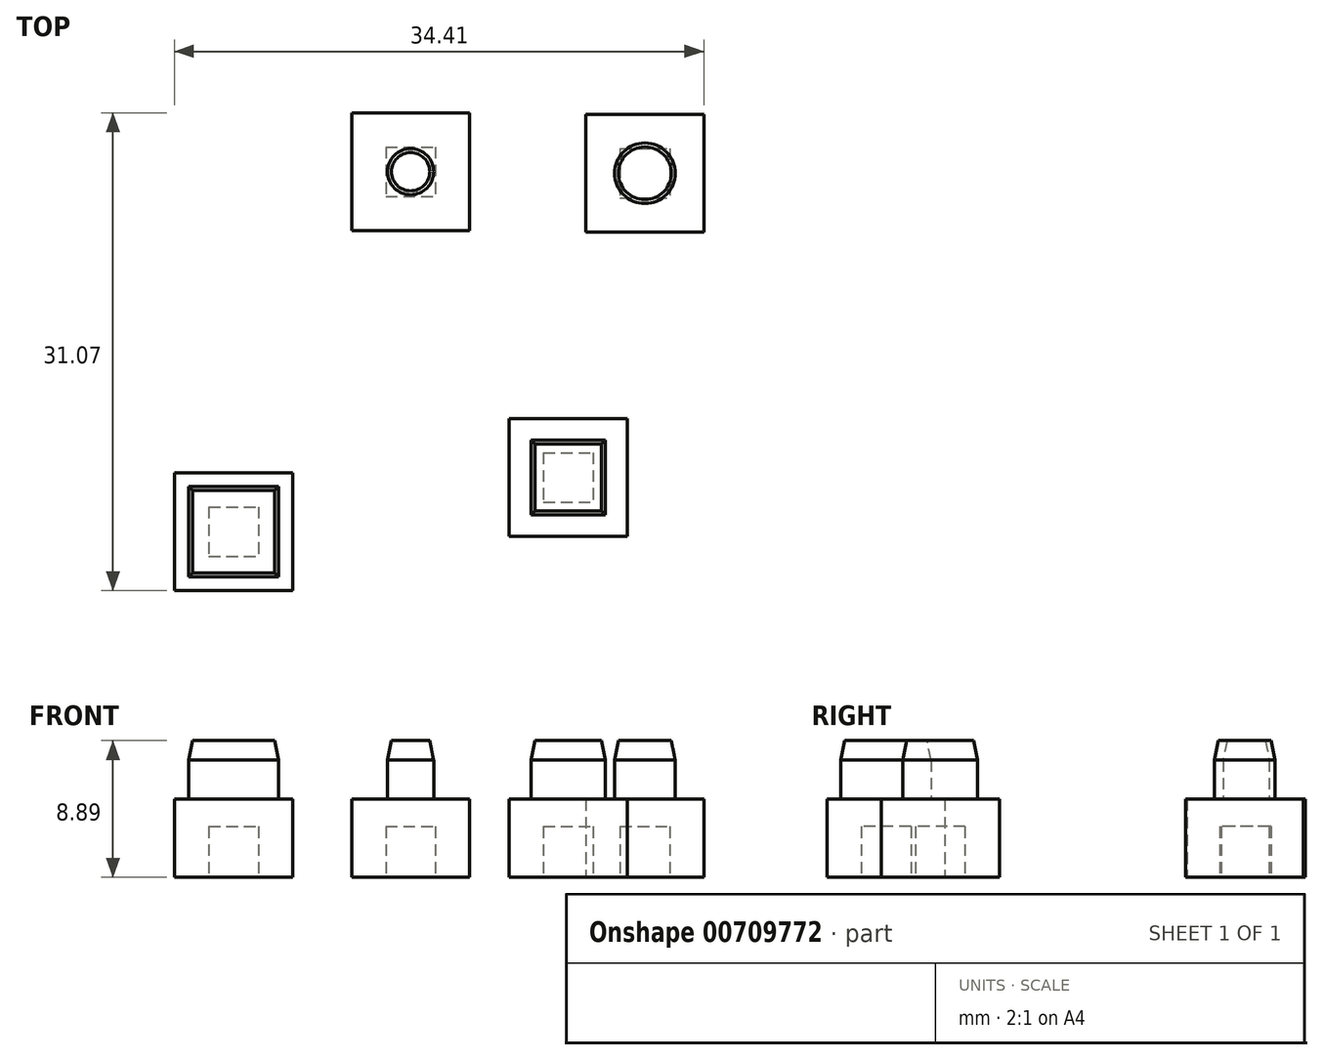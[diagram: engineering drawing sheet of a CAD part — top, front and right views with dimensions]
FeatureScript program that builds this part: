
annotation { "Feature Type Name" : "Feature", "Feature Type Description" : "" }
export const myFeature = defineFeature(function(context is Context, id is Id, definition is map)
    precondition{}
    {
        {
            var Q0;
            Q0=qCreatedBy(makeId("Top.planeOp"),FACE);
            var sketch = newSketch(context, id + "F0", { "sketchPlane" : qUnion([Q0])});
            skLineSegment(sketch, "E0.bottom", {"start": v(13.82, 29.65) * mm, "end": v(17.05, 29.65) * mm});
            skLineSegment(sketch, "E0.top", {"start": v(13.82, 26.43) * mm, "end": v(17.05, 26.43) * mm});
            skLineSegment(sketch, "E0.left", {"start": v(13.82, 29.65) * mm, "end": v(13.82, 26.43) * mm});
            skLineSegment(sketch, "E0.right", {"start": v(17.05, 29.65) * mm, "end": v(17.05, 26.43) * mm});
            skLineSegment(sketch, "E1.bottom", {"start": v(11.6, 24.2) * mm, "end": v(19.27, 24.2) * mm});
            skLineSegment(sketch, "E1.top", {"start": v(11.6, 31.87) * mm, "end": v(19.27, 31.87) * mm});
            skLineSegment(sketch, "E1.left", {"start": v(11.6, 24.2) * mm, "end": v(11.6, 31.87) * mm});
            skLineSegment(sketch, "E1.right", {"start": v(19.27, 24.2) * mm, "end": v(19.27, 31.87) * mm});
            skPoint(sketch, "E2", {"position": v(15.44, 28.04) * mm});
            skCircle(sketch, "E3", {"center": v(15.44, 28.04) * mm, "radius": 1.5 * mm});
            skLineSegment(sketch, "E4.bottom", {"start": v(2.31, 6.25) * mm, "end": v(5.54, 6.25) * mm});
            skLineSegment(sketch, "E4.top", {"start": v(2.31, 3.03) * mm, "end": v(5.54, 3.03) * mm});
            skLineSegment(sketch, "E4.left", {"start": v(2.31, 6.25) * mm, "end": v(2.31, 3.03) * mm});
            skLineSegment(sketch, "E4.right", {"start": v(5.54, 6.25) * mm, "end": v(5.54, 3.03) * mm});
            skLineSegment(sketch, "E5.bottom", {"start": v(0.1, 0.8) * mm, "end": v(7.76, 0.8) * mm});
            skLineSegment(sketch, "E5.top", {"start": v(0.1, 8.47) * mm, "end": v(7.76, 8.47) * mm});
            skLineSegment(sketch, "E5.left", {"start": v(0.1, 0.8) * mm, "end": v(0.1, 8.47) * mm});
            skLineSegment(sketch, "E5.right", {"start": v(7.76, 0.8) * mm, "end": v(7.76, 8.47) * mm});
            skPoint(sketch, "E6", {"position": v(3.93, 4.64) * mm});
            skLineSegment(sketch, "E7.bottom", {"start": v(24.07, 9.78) * mm, "end": v(27.3, 9.78) * mm});
            skLineSegment(sketch, "E7.top", {"start": v(24.07, 6.55) * mm, "end": v(27.3, 6.55) * mm});
            skLineSegment(sketch, "E7.left", {"start": v(24.07, 9.78) * mm, "end": v(24.07, 6.55) * mm});
            skLineSegment(sketch, "E7.right", {"start": v(27.3, 9.78) * mm, "end": v(27.3, 6.55) * mm});
            skLineSegment(sketch, "E8.bottom", {"start": v(21.84, 4.33) * mm, "end": v(29.52, 4.33) * mm});
            skLineSegment(sketch, "E8.top", {"start": v(21.84, 12) * mm, "end": v(29.52, 12) * mm});
            skLineSegment(sketch, "E8.left", {"start": v(21.84, 4.33) * mm, "end": v(21.84, 12) * mm});
            skLineSegment(sketch, "E8.right", {"start": v(29.52, 4.33) * mm, "end": v(29.52, 12) * mm});
            skPoint(sketch, "E9", {"position": v(25.68, 8.16) * mm});
            skLineSegment(sketch, "E10.bottom", {"start": v(29.05, 29.55) * mm, "end": v(32.28, 29.55) * mm});
            skLineSegment(sketch, "E10.top", {"start": v(29.05, 26.33) * mm, "end": v(32.28, 26.33) * mm});
            skLineSegment(sketch, "E10.left", {"start": v(29.05, 29.55) * mm, "end": v(29.05, 26.33) * mm});
            skLineSegment(sketch, "E10.right", {"start": v(32.28, 29.55) * mm, "end": v(32.28, 26.33) * mm});
            skLineSegment(sketch, "E11.bottom", {"start": v(26.83, 24.1) * mm, "end": v(34.5, 24.1) * mm});
            skLineSegment(sketch, "E11.top", {"start": v(26.83, 31.78) * mm, "end": v(34.5, 31.78) * mm});
            skLineSegment(sketch, "E11.left", {"start": v(26.83, 24.1) * mm, "end": v(26.83, 31.78) * mm});
            skLineSegment(sketch, "E11.right", {"start": v(34.5, 24.1) * mm, "end": v(34.5, 31.78) * mm});
            skPoint(sketch, "E12", {"position": v(30.66, 27.94) * mm});
            skCircle(sketch, "E13", {"center": v(30.66, 27.94) * mm, "radius": 1.97 * mm});
            skLineSegment(sketch, "E14.bottom", {"start": v(6.86, 7.57) * mm, "end": v(1, 7.57) * mm});
            skLineSegment(sketch, "E14.top", {"start": v(6.86, 1.7) * mm, "end": v(1, 1.7) * mm});
            skLineSegment(sketch, "E14.left", {"start": v(6.86, 7.57) * mm, "end": v(6.86, 1.7) * mm});
            skLineSegment(sketch, "E14.right", {"start": v(1, 7.57) * mm, "end": v(1, 1.7) * mm});
            skLineSegment(sketch, "E15.bottom", {"start": v(28.1, 10.59) * mm, "end": v(23.25, 10.59) * mm});
            skLineSegment(sketch, "E15.top", {"start": v(28.1, 5.74) * mm, "end": v(23.25, 5.74) * mm});
            skLineSegment(sketch, "E15.left", {"start": v(28.1, 10.59) * mm, "end": v(28.1, 5.74) * mm});
            skLineSegment(sketch, "E15.right", {"start": v(23.25, 10.59) * mm, "end": v(23.25, 5.74) * mm});
            skSolve(sketch);
        }
        {
            var Q0;
            Q0=makeQuery(id+"F0.imprint","IMPRINT",FACE,{"disambiguationData":[TD([[makeQuery(id+"F0.imprint","IMPRINT",EDGE,{"derivedFrom":sQuery(id+"F0.wireOp",EDGE,"E4.bottom")}),1.0]])]});
            var Q1;
            Q1=makeQuery(id+"F0.imprint","IMPRINT",FACE,{"disambiguationData":[TD([[makeQuery(id+"F0.imprint","IMPRINT",EDGE,{"derivedFrom":sQuery(id+"F0.wireOp",EDGE,"E11.bottom")}),1.0]])]});
            var Q2;
            Q2=makeQuery(id+"F0.imprint","IMPRINT",FACE,{"disambiguationData":[TD([[makeQuery(id+"F0.imprint","IMPRINT",EDGE,{"derivedFrom":sQuery(id+"F0.wireOp",EDGE,"E3")}),1.0]])]});
            var Q3;
            Q3=makeQuery(id+"F0.imprint","IMPRINT",FACE,{"disambiguationData":[TD([[makeQuery(id+"F0.imprint","IMPRINT",EDGE,{"derivedFrom":sQuery(id+"F0.wireOp",EDGE,"E0.bottom")}),1.0]])]});
            var Q4;
            {var subQ0=sQuery(id+"F0.wireOp",EDGE,"E13");var subQ7=sQuery(id+"F0.wireOp",EDGE,"E10.bottom");var subQ8=makeQuery(id+"F0.imprint","INTERSECT",VERTEX,{"disambiguationData":[OD(0.0)],"derivedFrom":[subQ7,subQ0]});Q4=makeQuery(id+"F0.imprint","IMPRINT",FACE,{"disambiguationData":[TD([[makeQuery(id+"F0.imprint","IMPRINT",EDGE,{"disambiguationData":[TD([[subQ8,-1.0]])],"derivedFrom":subQ7}),-1.0]])]});}
            var Q5;
            Q5=makeQuery(id+"F0.imprint","IMPRINT",FACE,{"disambiguationData":[TD([[makeQuery(id+"F0.imprint","IMPRINT",EDGE,{"derivedFrom":sQuery(id+"F0.wireOp",EDGE,"E8.bottom")}),1.0]])]});
            var Q6;
            Q6=makeQuery(id+"F0.imprint","IMPRINT",FACE,{"disambiguationData":[TD([[makeQuery(id+"F0.imprint","IMPRINT",EDGE,{"derivedFrom":sQuery(id+"F0.wireOp",EDGE,"E7.bottom")}),-1.0]])]});
            var Q7;
            Q7=makeQuery(id+"F0.imprint","IMPRINT",FACE,{"disambiguationData":[TD([[makeQuery(id+"F0.imprint","IMPRINT",EDGE,{"derivedFrom":sQuery(id+"F0.wireOp",EDGE,"E5.bottom")}),1.0]])]});
            var Q8;
            Q8=makeQuery(id+"F0.imprint","IMPRINT",FACE,{"disambiguationData":[TD([[makeQuery(id+"F0.imprint","IMPRINT",EDGE,{"derivedFrom":sQuery(id+"F0.wireOp",EDGE,"E7.bottom")}),1.0]])]});
            var Q9;
            Q9=makeQuery(id+"F0.imprint","IMPRINT",FACE,{"disambiguationData":[TD([[makeQuery(id+"F0.imprint","IMPRINT",EDGE,{"derivedFrom":sQuery(id+"F0.wireOp",EDGE,"E4.bottom")}),-1.0]])]});
            var Q10;
            {var subQ0=sQuery(id+"F0.wireOp",EDGE,"E13");var subQ1=sQuery(id+"F0.wireOp",EDGE,"E10.left");var subQ2=makeQuery(id+"F0.imprint","INTERSECT",VERTEX,{"disambiguationData":[OD(0.0)],"derivedFrom":[subQ1,subQ0]});Q10=makeQuery(id+"F0.imprint","IMPRINT",FACE,{"disambiguationData":[TD([[makeQuery(id+"F0.imprint","IMPRINT",EDGE,{"disambiguationData":[TD([[subQ2,-1.0]])],"derivedFrom":subQ1}),-1.0]])]});}
            var Q11;
            Q11=makeQuery(id+"F0.imprint","IMPRINT",FACE,{"disambiguationData":[TD([[makeQuery(id+"F0.imprint","IMPRINT",EDGE,{"derivedFrom":sQuery(id+"F0.wireOp",EDGE,"E0.bottom")}),-1.0]])]});
            var Q12;
            {var subQ0=sQuery(id+"F0.wireOp",EDGE,"E13");var subQ1=sQuery(id+"F0.wireOp",EDGE,"E10.right");var subQ2=makeQuery(id+"F0.imprint","INTERSECT",VERTEX,{"disambiguationData":[OD(0.0)],"derivedFrom":[subQ1,subQ0]});Q12=makeQuery(id+"F0.imprint","IMPRINT",FACE,{"disambiguationData":[TD([[makeQuery(id+"F0.imprint","IMPRINT",EDGE,{"disambiguationData":[TD([[subQ2,-1.0]])],"derivedFrom":subQ1}),1.0]])]});}
            var Q13;
            {var subQ0=sQuery(id+"F0.wireOp",EDGE,"E13");var subQ1=sQuery(id+"F0.wireOp",EDGE,"E10.top");var subQ2=makeQuery(id+"F0.imprint","INTERSECT",VERTEX,{"disambiguationData":[OD(0.0)],"derivedFrom":[subQ1,subQ0]});Q13=makeQuery(id+"F0.imprint","IMPRINT",FACE,{"disambiguationData":[TD([[makeQuery(id+"F0.imprint","IMPRINT",EDGE,{"disambiguationData":[TD([[subQ2,-1.0]])],"derivedFrom":subQ1}),-1.0]])]});}
            var Q14;
            {var subQ0=sQuery(id+"F0.wireOp",EDGE,"E13");var subQ1=sQuery(id+"F0.wireOp",EDGE,"E10.bottom");var subQ2=makeQuery(id+"F0.imprint","INTERSECT",VERTEX,{"disambiguationData":[OD(0.0)],"derivedFrom":[subQ1,subQ0]});Q14=makeQuery(id+"F0.imprint","IMPRINT",FACE,{"disambiguationData":[TD([[makeQuery(id+"F0.imprint","IMPRINT",EDGE,{"disambiguationData":[TD([[subQ2,-1.0]])],"derivedFrom":subQ1}),1.0]])]});}
            var Q15;
            {var subQ0=sQuery(id+"F0.wireOp",EDGE,"E10.left");var subQ1=sQuery(id+"F0.wireOp",EDGE,"E10.top");var subQ2=makeQuery(id+"F0.imprint","INTERSECT",VERTEX,{"derivedFrom":[subQ1,subQ0]});Q15=makeQuery(id+"F0.imprint","IMPRINT",FACE,{"disambiguationData":[TD([[makeQuery(id+"F0.imprint","IMPRINT",EDGE,{"disambiguationData":[TD([[subQ2,-1.0]])],"derivedFrom":subQ1}),1.0]])]});}
            var Q16;
            {var subQ0=sQuery(id+"F0.wireOp",EDGE,"E10.left");var subQ1=sQuery(id+"F0.wireOp",EDGE,"E10.bottom");var subQ2=makeQuery(id+"F0.imprint","INTERSECT",VERTEX,{"derivedFrom":[subQ1,subQ0]});Q16=makeQuery(id+"F0.imprint","IMPRINT",FACE,{"disambiguationData":[TD([[makeQuery(id+"F0.imprint","IMPRINT",EDGE,{"disambiguationData":[TD([[subQ2,-1.0]])],"derivedFrom":subQ1}),-1.0]])]});}
            var Q17;
            {var subQ0=sQuery(id+"F0.wireOp",EDGE,"E10.right");var subQ1=sQuery(id+"F0.wireOp",EDGE,"E10.bottom");var subQ2=makeQuery(id+"F0.imprint","INTERSECT",VERTEX,{"derivedFrom":[subQ1,subQ0]});Q17=makeQuery(id+"F0.imprint","IMPRINT",FACE,{"disambiguationData":[TD([[makeQuery(id+"F0.imprint","IMPRINT",EDGE,{"disambiguationData":[TD([[subQ2,1.0]])],"derivedFrom":subQ1}),-1.0]])]});}
            var Q18;
            {var subQ0=sQuery(id+"F0.wireOp",EDGE,"E10.right");var subQ1=sQuery(id+"F0.wireOp",EDGE,"E10.top");var subQ2=makeQuery(id+"F0.imprint","INTERSECT",VERTEX,{"derivedFrom":[subQ1,subQ0]});Q18=makeQuery(id+"F0.imprint","IMPRINT",FACE,{"disambiguationData":[TD([[makeQuery(id+"F0.imprint","IMPRINT",EDGE,{"disambiguationData":[TD([[subQ2,1.0]])],"derivedFrom":subQ1}),1.0]])]});}
            extrude(context, id + "F1", {"entities" : qUnion([Q0, Q1, Q2, Q3, Q4, Q5, Q6, Q7, Q8, Q9, Q10, Q11, Q12, Q13, Q14, Q15, Q16, Q17, Q18]), "depth" : 5.08 * mm, "offsetDistance" : 25.4 * mm});
        }
        {
            var Q0;
            {var subQ0=sQuery(id+"F0.wireOp",EDGE,"E13");var subQ1=sQuery(id+"F0.wireOp",EDGE,"E10.top");var subQ2=makeQuery(id+"F0.imprint","INTERSECT",VERTEX,{"disambiguationData":[OD(0.0)],"derivedFrom":[subQ1,subQ0]});Q0=makeQuery(id+"F0.imprint","IMPRINT",FACE,{"disambiguationData":[TD([[makeQuery(id+"F0.imprint","IMPRINT",EDGE,{"disambiguationData":[TD([[subQ2,-1.0]])],"derivedFrom":subQ1}),-1.0]])]});}
            var Q1;
            {var subQ0=sQuery(id+"F0.wireOp",EDGE,"E13");var subQ7=sQuery(id+"F0.wireOp",EDGE,"E10.bottom");var subQ8=makeQuery(id+"F0.imprint","INTERSECT",VERTEX,{"disambiguationData":[OD(0.0)],"derivedFrom":[subQ7,subQ0]});Q1=makeQuery(id+"F0.imprint","IMPRINT",FACE,{"disambiguationData":[TD([[makeQuery(id+"F0.imprint","IMPRINT",EDGE,{"disambiguationData":[TD([[subQ8,-1.0]])],"derivedFrom":subQ7}),-1.0]])]});}
            var Q2;
            {var subQ0=sQuery(id+"F0.wireOp",EDGE,"E13");var subQ1=sQuery(id+"F0.wireOp",EDGE,"E10.left");var subQ2=makeQuery(id+"F0.imprint","INTERSECT",VERTEX,{"disambiguationData":[OD(0.0)],"derivedFrom":[subQ1,subQ0]});Q2=makeQuery(id+"F0.imprint","IMPRINT",FACE,{"disambiguationData":[TD([[makeQuery(id+"F0.imprint","IMPRINT",EDGE,{"disambiguationData":[TD([[subQ2,-1.0]])],"derivedFrom":subQ1}),-1.0]])]});}
            var Q3;
            {var subQ0=sQuery(id+"F0.wireOp",EDGE,"E13");var subQ1=sQuery(id+"F0.wireOp",EDGE,"E10.bottom");var subQ2=makeQuery(id+"F0.imprint","INTERSECT",VERTEX,{"disambiguationData":[OD(0.0)],"derivedFrom":[subQ1,subQ0]});Q3=makeQuery(id+"F0.imprint","IMPRINT",FACE,{"disambiguationData":[TD([[makeQuery(id+"F0.imprint","IMPRINT",EDGE,{"disambiguationData":[TD([[subQ2,-1.0]])],"derivedFrom":subQ1}),1.0]])]});}
            var Q4;
            {var subQ0=sQuery(id+"F0.wireOp",EDGE,"E13");var subQ1=sQuery(id+"F0.wireOp",EDGE,"E10.right");var subQ2=makeQuery(id+"F0.imprint","INTERSECT",VERTEX,{"disambiguationData":[OD(0.0)],"derivedFrom":[subQ1,subQ0]});Q4=makeQuery(id+"F0.imprint","IMPRINT",FACE,{"disambiguationData":[TD([[makeQuery(id+"F0.imprint","IMPRINT",EDGE,{"disambiguationData":[TD([[subQ2,-1.0]])],"derivedFrom":subQ1}),1.0]])]});}
            var Q5;
            Q5=sQuery(id+"F0.wireOp",EDGE,"E13");
            extrude(context, id + "F2", {"entities" : qUnion([Q0, Q1, Q2, Q3, Q4]), "operationType" : NewBodyOperationType.ADD, "surfaceEntities" : qUnion([Q5]), "depth" : 8.9 * mm, "offsetDistance" : 25.4 * mm});
        }
        {
            var Q0;
            Q0=makeQuery(id+"F0.imprint","IMPRINT",FACE,{"disambiguationData":[TD([[makeQuery(id+"F0.imprint","IMPRINT",EDGE,{"derivedFrom":sQuery(id+"F0.wireOp",EDGE,"E3")}),1.0]])]});
            extrude(context, id + "F3", {"entities" : qUnion([Q0]), "operationType" : NewBodyOperationType.ADD, "depth" : 8.9 * mm, "offsetDistance" : 25.4 * mm});
        }
        {
            var Q0;
            Q0=makeQuery(id+"F0.imprint","IMPRINT",FACE,{"disambiguationData":[TD([[makeQuery(id+"F0.imprint","IMPRINT",EDGE,{"derivedFrom":sQuery(id+"F0.wireOp",EDGE,"E7.bottom")}),1.0]])]});
            var Q1;
            Q1=makeQuery(id+"F0.imprint","IMPRINT",FACE,{"disambiguationData":[TD([[makeQuery(id+"F0.imprint","IMPRINT",EDGE,{"derivedFrom":sQuery(id+"F0.wireOp",EDGE,"E7.bottom")}),-1.0]])]});
            extrude(context, id + "F4", {"entities" : qUnion([Q0, Q1]), "operationType" : NewBodyOperationType.ADD, "depth" : 8.9 * mm, "offsetDistance" : 25.4 * mm});
        }
        {
            var Q0;
            Q0=makeQuery(id+"F0.imprint","IMPRINT",FACE,{"disambiguationData":[TD([[makeQuery(id+"F0.imprint","IMPRINT",EDGE,{"derivedFrom":sQuery(id+"F0.wireOp",EDGE,"E4.bottom")}),1.0]])]});
            var Q1;
            Q1=makeQuery(id+"F0.imprint","IMPRINT",FACE,{"disambiguationData":[TD([[makeQuery(id+"F0.imprint","IMPRINT",EDGE,{"derivedFrom":sQuery(id+"F0.wireOp",EDGE,"E4.bottom")}),-1.0]])]});
            extrude(context, id + "F5", {"entities" : qUnion([Q0, Q1]), "operationType" : NewBodyOperationType.ADD, "depth" : 8.9 * mm, "offsetDistance" : 25.4 * mm});
        }
        {
            var Q0;
            Q0=makeQuery(id+"F5.opExtrude","CAP_FACE",FACE,{"disambiguationData":[OSD([sQuery(id+"F0.wireOp",EDGE,"E14.bottom"),sQuery(id+"F0.wireOp",EDGE,"E14.top"),sQuery(id+"F0.wireOp",EDGE,"E14.left"),sQuery(id+"F0.wireOp",EDGE,"E14.right")])],"isStart":false});
            var Q1;
            Q1=makeQuery(id+"F3.opExtrude","CAP_FACE",FACE,{"disambiguationData":[OSD([sQuery(id+"F0.wireOp",EDGE,"E3")])],"isStart":false});
            var Q2;
            Q2=makeQuery(id+"F2.opExtrude","CAP_FACE",FACE,{"disambiguationData":[OSD([sQuery(id+"F0.wireOp",EDGE,"E13")])],"isStart":false});
            var Q3;
            Q3=makeQuery(id+"F4.opExtrude","CAP_FACE",FACE,{"disambiguationData":[OSD([sQuery(id+"F0.wireOp",EDGE,"E15.bottom"),sQuery(id+"F0.wireOp",EDGE,"E15.top"),sQuery(id+"F0.wireOp",EDGE,"E15.left"),sQuery(id+"F0.wireOp",EDGE,"E15.right")])],"isStart":false});
            chamfer(context, id + "F6", {"entities" : qUnion([Q0, Q1, Q2, Q3]), "chamferType" : ChamferType.TWO_OFFSETS, "width1" : 0.25 * mm, "oppositeDirection" : false, "width2" : 1.27 * mm, "tangentPropagation" : true});
        }
        {
            var Q0;
            {var subQ0=sQuery(id+"F0.wireOp",EDGE,"E13");var subQ7=sQuery(id+"F0.wireOp",EDGE,"E10.bottom");var subQ8=makeQuery(id+"F0.imprint","INTERSECT",VERTEX,{"disambiguationData":[OD(0.0)],"derivedFrom":[subQ7,subQ0]});Q0=makeQuery(id+"F0.imprint","IMPRINT",FACE,{"disambiguationData":[TD([[makeQuery(id+"F0.imprint","IMPRINT",EDGE,{"disambiguationData":[TD([[subQ8,-1.0]])],"derivedFrom":subQ7}),-1.0]])]});}
            var Q1;
            {var subQ0=sQuery(id+"F0.wireOp",EDGE,"E10.left");var subQ1=sQuery(id+"F0.wireOp",EDGE,"E10.top");var subQ2=makeQuery(id+"F0.imprint","INTERSECT",VERTEX,{"derivedFrom":[subQ1,subQ0]});Q1=makeQuery(id+"F0.imprint","IMPRINT",FACE,{"disambiguationData":[TD([[makeQuery(id+"F0.imprint","IMPRINT",EDGE,{"disambiguationData":[TD([[subQ2,-1.0]])],"derivedFrom":subQ1}),1.0]])]});}
            var Q2;
            {var subQ0=sQuery(id+"F0.wireOp",EDGE,"E10.right");var subQ1=sQuery(id+"F0.wireOp",EDGE,"E10.top");var subQ2=makeQuery(id+"F0.imprint","INTERSECT",VERTEX,{"derivedFrom":[subQ1,subQ0]});Q2=makeQuery(id+"F0.imprint","IMPRINT",FACE,{"disambiguationData":[TD([[makeQuery(id+"F0.imprint","IMPRINT",EDGE,{"disambiguationData":[TD([[subQ2,1.0]])],"derivedFrom":subQ1}),1.0]])]});}
            var Q3;
            {var subQ0=sQuery(id+"F0.wireOp",EDGE,"E10.right");var subQ1=sQuery(id+"F0.wireOp",EDGE,"E10.bottom");var subQ2=makeQuery(id+"F0.imprint","INTERSECT",VERTEX,{"derivedFrom":[subQ1,subQ0]});Q3=makeQuery(id+"F0.imprint","IMPRINT",FACE,{"disambiguationData":[TD([[makeQuery(id+"F0.imprint","IMPRINT",EDGE,{"disambiguationData":[TD([[subQ2,1.0]])],"derivedFrom":subQ1}),-1.0]])]});}
            var Q4;
            {var subQ0=sQuery(id+"F0.wireOp",EDGE,"E10.left");var subQ1=sQuery(id+"F0.wireOp",EDGE,"E10.bottom");var subQ2=makeQuery(id+"F0.imprint","INTERSECT",VERTEX,{"derivedFrom":[subQ1,subQ0]});Q4=makeQuery(id+"F0.imprint","IMPRINT",FACE,{"disambiguationData":[TD([[makeQuery(id+"F0.imprint","IMPRINT",EDGE,{"disambiguationData":[TD([[subQ2,-1.0]])],"derivedFrom":subQ1}),-1.0]])]});}
            extrude(context, id + "F7", {"entities" : qUnion([Q0, Q1, Q2, Q3, Q4]), "operationType" : NewBodyOperationType.REMOVE, "depth" : 3.3 * mm, "offsetDistance" : 25.4 * mm});
        }
        {
            var Q0;
            Q0=makeQuery(id+"F0.imprint","IMPRINT",FACE,{"disambiguationData":[TD([[makeQuery(id+"F0.imprint","IMPRINT",EDGE,{"derivedFrom":sQuery(id+"F0.wireOp",EDGE,"E0.bottom")}),-1.0]])]});
            var Q1;
            Q1=makeQuery(id+"F0.imprint","IMPRINT",FACE,{"disambiguationData":[TD([[makeQuery(id+"F0.imprint","IMPRINT",EDGE,{"derivedFrom":sQuery(id+"F0.wireOp",EDGE,"E3")}),1.0]])]});
            extrude(context, id + "F8", {"entities" : qUnion([Q0, Q1]), "operationType" : NewBodyOperationType.REMOVE, "depth" : 3.3 * mm, "offsetDistance" : 25.4 * mm});
        }
        {
            var Q0;
            Q0=makeQuery(id+"F0.imprint","IMPRINT",FACE,{"disambiguationData":[TD([[makeQuery(id+"F0.imprint","IMPRINT",EDGE,{"derivedFrom":sQuery(id+"F0.wireOp",EDGE,"E7.bottom")}),-1.0]])]});
            extrude(context, id + "F9", {"entities" : qUnion([Q0]), "operationType" : NewBodyOperationType.REMOVE, "depth" : 3.3 * mm, "offsetDistance" : 25.4 * mm});
        }
        {
            var Q0;
            Q0=makeQuery(id+"F0.imprint","IMPRINT",FACE,{"disambiguationData":[TD([[makeQuery(id+"F0.imprint","IMPRINT",EDGE,{"derivedFrom":sQuery(id+"F0.wireOp",EDGE,"E4.bottom")}),-1.0]])]});
            extrude(context, id + "F10", {"entities" : qUnion([Q0]), "operationType" : NewBodyOperationType.REMOVE, "depth" : 3.3 * mm, "offsetDistance" : 25.4 * mm});
        }
    });
